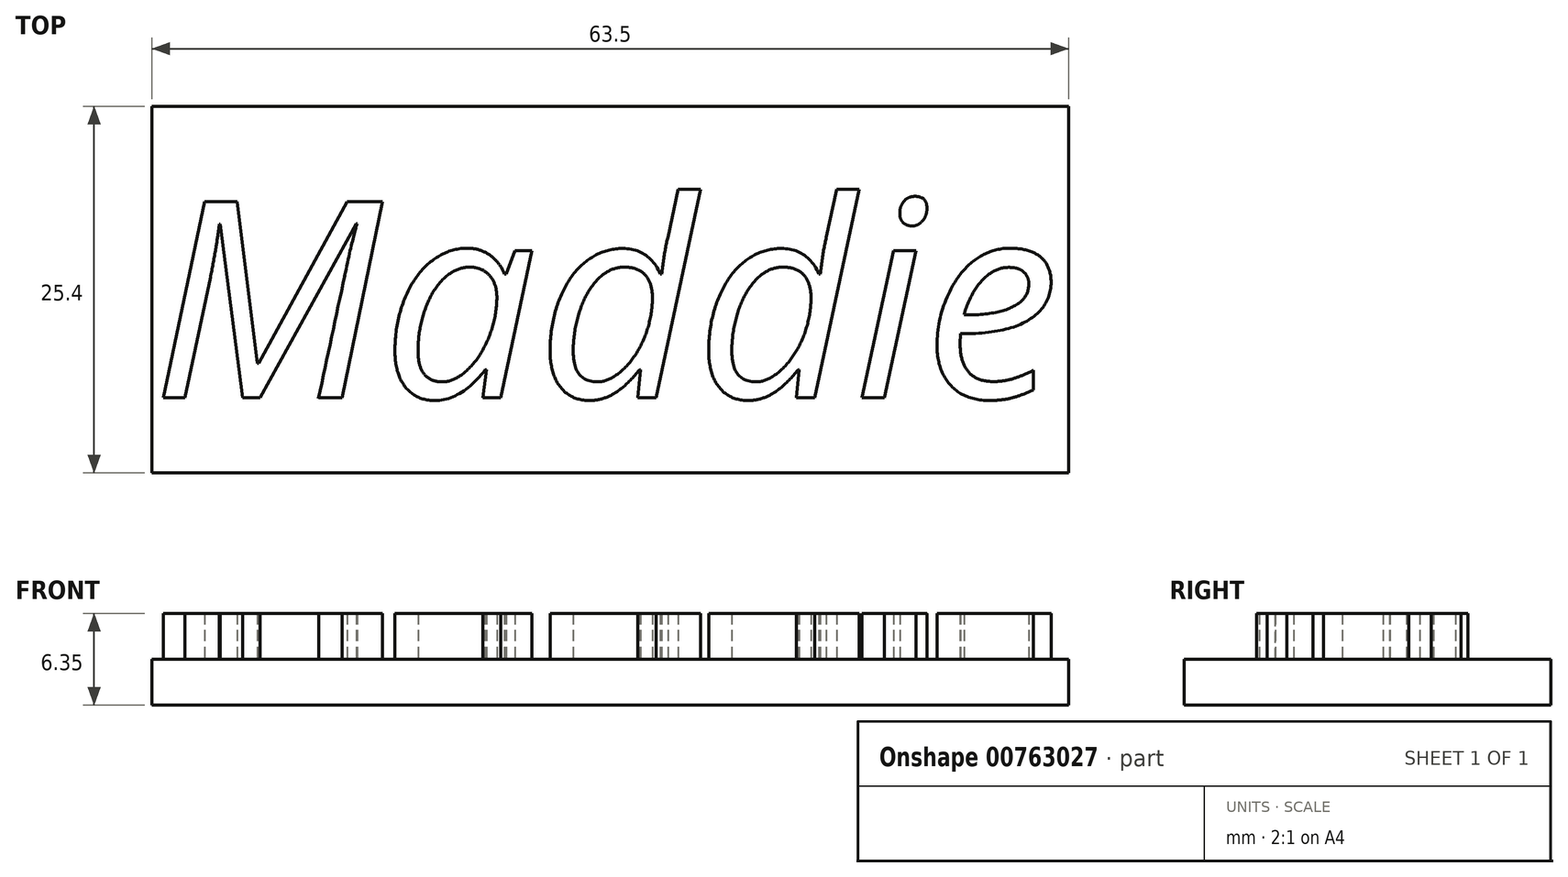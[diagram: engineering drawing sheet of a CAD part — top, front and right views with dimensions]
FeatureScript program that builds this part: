
annotation { "Feature Type Name" : "Feature", "Feature Type Description" : "" }
export const myFeature = defineFeature(function(context is Context, id is Id, definition is map)
    precondition{}
    {
        {
            var Q0;
            Q0=qCreatedBy(makeId("Top.planeOp"),FACE);
            var sketch = newSketch(context, id + "F0", { "sketchPlane" : qUnion([Q0])});
            skLineSegment(sketch, "E0.bottom", {"start": v(0, 0) * mm, "end": v(63.5, 0) * mm});
            skLineSegment(sketch, "E0.top", {"start": v(0, 25.4) * mm, "end": v(63.5, 25.4) * mm});
            skLineSegment(sketch, "E0.left", {"start": v(0, 0) * mm, "end": v(0, 25.4) * mm});
            skLineSegment(sketch, "E0.right", {"start": v(63.5, 0) * mm, "end": v(63.5, 25.4) * mm});
            skSolve(sketch);
        }
        {
            var Q0;
            Q0 = qSketchRegion(id + "F0", true);
            extrude(context, id + "F1", {"entities" : qUnion([Q0]), "depth" : 3.17 * mm, "offsetDistance" : 25.4 * mm});
        }
        {
            var Q0;
            Q0=makeQuery(id+"F1.opExtrude","CAP_FACE",FACE,{"disambiguationData":[OSD([sQuery(id+"F0.wireOp",EDGE,"E0.bottom"),sQuery(id+"F0.wireOp",EDGE,"E0.top"),sQuery(id+"F0.wireOp",EDGE,"E0.left"),sQuery(id+"F0.wireOp",EDGE,"E0.right")])],"isStart":false});
            var sketch = newSketch(context, id + "F2", { "sketchPlane" : qUnion([Q0])});
            skText(sketch, "E1", { "text": "Maddie ", "fontName": "OpenSans-Italic.ttf"});
            const initialGuessF2  = {"E1": [0, 0.0052, 1, 0, 0.0137]};
            skSetInitialGuess(sketch, initialGuessF2);
            skSolve(sketch);
        }
        {
            var Q0;
            Q0 = qSketchRegion(id + "F2", true);
            extrude(context, id + "F3", {"entities" : qUnion([Q0]), "operationType" : NewBodyOperationType.ADD, "depth" : 3.17 * mm, "offsetDistance" : 25.4 * mm});
        }
    });
